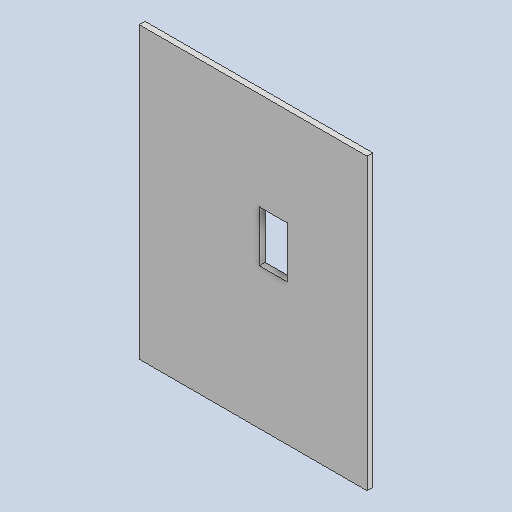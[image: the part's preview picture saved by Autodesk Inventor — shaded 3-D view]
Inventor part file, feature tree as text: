
AUTODESK INVENTOR PART (.ipt)
format: ipt  version: 2022 (Build 260153000, 153)  size: 113,152 bytes
history: native  units: mm
features: reference x6, other x4, extrude x3, sketch x3, projected_geometry x1
ambient origin geometry x8: Origin, YZ Plane, XZ Plane, XY Plane, X Axis, Y Axis, Z Axis, Center Point
bodies: Solid1 (feature_tree)
feature tree (17):
  extrude  "Extrusion1"  Depth=0.2mm TaperAngle=0.0deg
  extrude  "Extrusion2"  [1 undecoded]
  extrude  "Extrusion3"  [1 undecoded]
  sketch  "Sketch1"  dims[d0=0.7mm d1=0.0mm d2=0.2mm d3=0.0mm]
  reference  "Reference1"
  reference  "Reference2"
  reference  "Reference3"
  reference  "Reference4"
  reference  "Reference5"
  sketch  "Sketch2"  dims[d4=0.0mm d5=0.0mm]
  projected_geometry  "Projected Loop1"
  sketch  "Sketch3"
  reference  "Reference6"
  other  "<userpath>\Documents\Inventor\NanoSumo\Przekładnia.iam"
  other  "Przekładnia.iam"
  other  "TOF_VL53L0X (1):1"
  other  "pcb:1"
note: 2 required parameter values undecoded (feature->parameter linkage not recoverable at this tier; creation-order binding heuristic only, values carry confidence <= 0.55)
